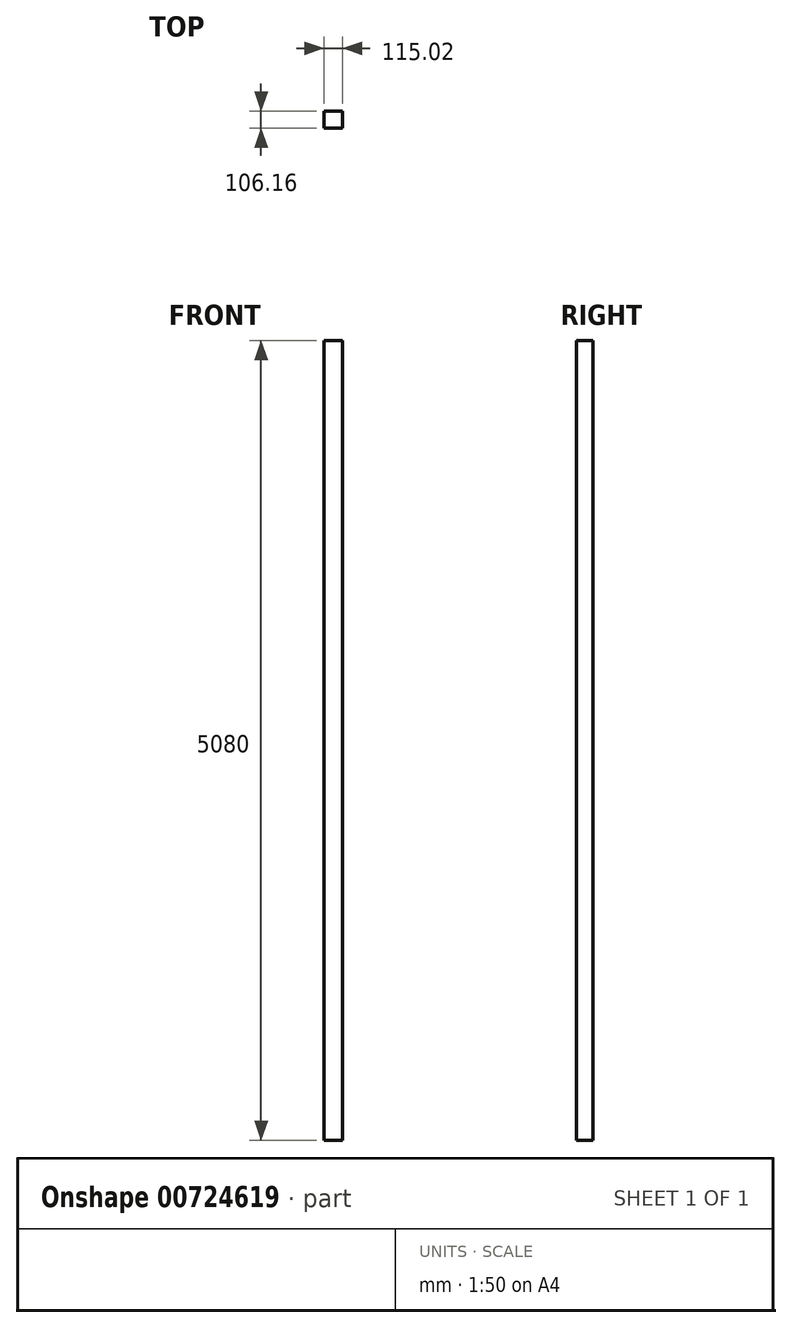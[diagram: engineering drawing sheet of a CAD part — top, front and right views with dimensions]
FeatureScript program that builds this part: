
annotation { "Feature Type Name" : "Feature", "Feature Type Description" : "" }
export const myFeature = defineFeature(function(context is Context, id is Id, definition is map)
    precondition{}
    {
        {
            var Q0;
            Q0=qCreatedBy(makeId("Top.planeOp"),FACE);
            var sketch = newSketch(context, id + "F0", { "sketchPlane" : qUnion([Q0])});
            skLineSegment(sketch, "E0.bottom", {"start": v(57.51, -53.08) * mm, "end": v(-57.51, -53.08) * mm});
            skLineSegment(sketch, "E0.top", {"start": v(57.51, 53.08) * mm, "end": v(-57.51, 53.08) * mm});
            skLineSegment(sketch, "E0.left", {"start": v(57.51, -53.08) * mm, "end": v(57.51, 53.08) * mm});
            skLineSegment(sketch, "E0.right", {"start": v(-57.51, -53.08) * mm, "end": v(-57.51, 53.08) * mm});
            skPoint(sketch, "E0.middle", {"position": v(0, 0) * mm});
            skSolve(sketch);
        }
        {
            var Q0;
            Q0 = qSketchRegion(id + "F0", true);
            extrude(context, id + "F1", {"entities" : qUnion([Q0]), "depth" : 5080 * mm, "offsetDistance" : 25.4 * mm});
        }
    });
